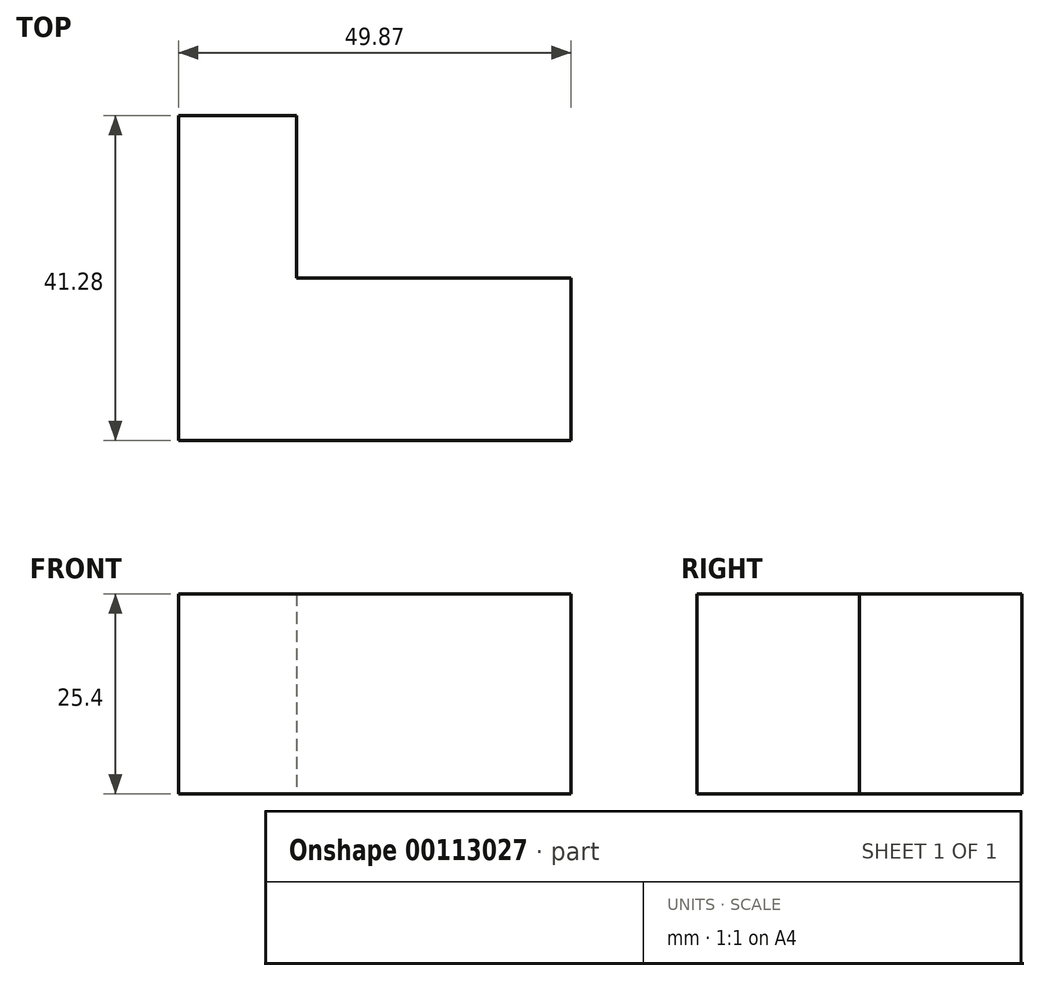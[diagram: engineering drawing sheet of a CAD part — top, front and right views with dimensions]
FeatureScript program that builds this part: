
annotation { "Feature Type Name" : "Feature", "Feature Type Description" : "" }
export const myFeature = defineFeature(function(context is Context, id is Id, definition is map)
    precondition{}
    {
        {
            var Q0;
            Q0=qCreatedBy(makeId("Top.planeOp"),FACE);
            var sketch = newSketch(context, id + "F0", { "sketchPlane" : qUnion([Q0])});
            skLineSegment(sketch, "E0.bottom", {"start": v(0, 0) * mm, "end": v(49.87, 0) * mm});
            skLineSegment(sketch, "E0.top", {"start": v(0, -41.28) * mm, "end": v(49.87, -41.28) * mm});
            skLineSegment(sketch, "E0.left", {"start": v(0, 0) * mm, "end": v(0, -41.28) * mm});
            skLineSegment(sketch, "E0.right", {"start": v(49.87, 0) * mm, "end": v(49.87, -41.28) * mm});
            skLineSegment(sketch, "E1.bottom", {"start": v(49.87, -20.64) * mm, "end": v(15, -20.64) * mm});
            skLineSegment(sketch, "E1.top", {"start": v(49.87, 56.53) * mm, "end": v(15, 56.53) * mm});
            skLineSegment(sketch, "E1.left", {"start": v(49.87, -20.64) * mm, "end": v(49.87, 56.53) * mm});
            skLineSegment(sketch, "E1.right", {"start": v(15, -20.64) * mm, "end": v(15, 56.53) * mm});
            skSolve(sketch);
        }
        {
            var Q0;
            Q0=makeQuery(id+"F0.imprint","IMPRINT",FACE,{"disambiguationData":[TD([[makeQuery(id+"F0.imprint","IMPRINT",EDGE,{"derivedFrom":sQuery(id+"F0.wireOp",EDGE,"E0.top")}),1.0]])]});
            extrude(context, id + "F1", {"entities" : qUnion([Q0]), "depth" : 25.4 * mm});
        }
        {
            var Q0;
            Q0=makeQuery(id+"F1.opExtrude","CAP_FACE",FACE,{"disambiguationData":[OSD([sQuery(id+"F0.wireOp",EDGE,"E0.bottom"),sQuery(id+"F0.wireOp",EDGE,"E0.top"),sQuery(id+"F0.wireOp",EDGE,"E0.left"),sQuery(id+"F0.wireOp",EDGE,"E0.right"),sQuery(id+"F0.wireOp",EDGE,"E1.bottom"),sQuery(id+"F0.wireOp",EDGE,"E1.right")])],"isStart":false});
            var Q1;
            Q1=makeQuery(id+"F1.opExtrude","SWEPT_EDGE",EDGE,{"disambiguationData":[OSD([sQuery(id+"F0.wireOp",EDGE,"E0.top"),sQuery(id+"F0.wireOp",EDGE,"E0.right")])]});
            sweep(context, id + "F2", {"operationType" : NewBodyOperationType.ADD, "profiles" : qUnion([Q0]), "path" : qUnion([Q1])});
        }
    });
